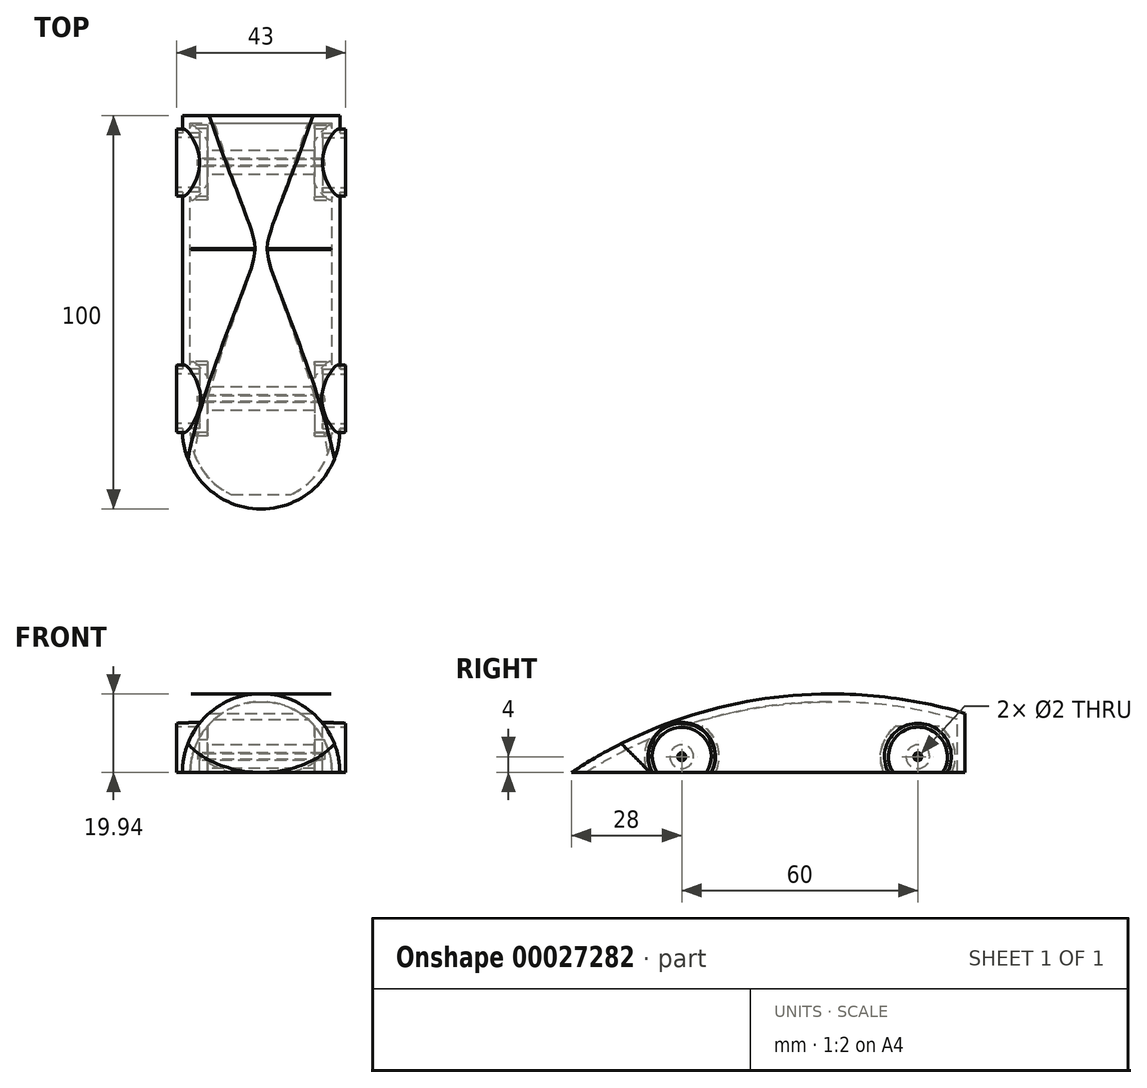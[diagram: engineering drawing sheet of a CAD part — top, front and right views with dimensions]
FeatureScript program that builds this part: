
annotation { "Feature Type Name" : "Feature", "Feature Type Description" : "" }
export const myFeature = defineFeature(function(context is Context, id is Id, definition is map)
    precondition{}
    {
        {
            var Q0;
            Q0=qCreatedBy(makeId("Top.planeOp"),FACE);
            var sketch = newSketch(context, id + "F0", { "sketchPlane" : qUnion([Q0])});
            skPoint(sketch, "E0.rect.middle", {"position": v(0, 0) * mm});
            skLineSegment(sketch, "E1.rect.bottom", {"start": v(-20, 50) * mm, "end": v(20, 50) * mm});
            skLineSegment(sketch, "E1.rect.top", {"start": v(-20, -50) * mm, "end": v(20, -50) * mm});
            skLineSegment(sketch, "E1.rect.left", {"start": v(-20, 50) * mm, "end": v(-20, -50) * mm});
            skLineSegment(sketch, "E1.rect.right", {"start": v(20, 50) * mm, "end": v(20, -50) * mm});
            skSolve(sketch);
        }
        {
            var Q0;
            Q0 = qSketchRegion(id + "F0", true);
            extrude(context, id + "F1", {"entities" : qUnion([Q0]), "depth" : 30 * mm});
        }
        {
            var Q0;
            Q0=makeQuery(id+"F1.opExtrude","SWEPT_FACE",FACE,{"disambiguationData":[OSD([sQuery(id+"F0.wireOp",EDGE,"E1.rect.top")])]});
            var sketch = newSketch(context, id + "F2", { "sketchPlane" : qUnion([Q0])});
            skArc(sketch, "E2", {"start": v(20, 15) * mm, "mid": v(0, 30) * mm, "end": v(-20, 15) * mm});
            skLineSegment(sketch, "E3", {"start": v(-20, 15) * mm, "end": v(-20, 30) * mm});
            skLineSegment(sketch, "E4", {"start": v(-20, 30) * mm, "end": v(20, 30) * mm});
            skLineSegment(sketch, "E5", {"start": v(20, 30) * mm, "end": v(20, 15) * mm});
            skSolve(sketch);
        }
        {
            var Q0;
            Q0 = qSketchRegion(id + "F2", true);
            extrude(context, id + "F3", {"entities" : qUnion([Q0]), "operationType" : NewBodyOperationType.REMOVE, "endBound" : BoundingType.THROUGH_ALL, "oppositeDirection" : true, "depth" : 25 * mm});
        }
        {
            var Q0;
            Q0=makeQuery(id+"F1.opExtrude","SWEPT_FACE",FACE,{"disambiguationData":[OSD([sQuery(id+"F0.wireOp",EDGE,"E1.rect.right")])]});
            var sketch = newSketch(context, id + "F4", { "sketchPlane" : qUnion([Q0])});
            skArc(sketch, "E6", {"start": v(50, 15) * mm, "mid": v(-1.67, 18.62) * mm, "end": v(-50, 0) * mm});
            skLineSegment(sketch, "E7.0", {"start": v(-50, 15) * mm, "end": v(-50, 30) * mm});
            skLineSegment(sketch, "E8", {"start": v(-50, 30) * mm, "end": v(50, 30) * mm});
            skLineSegment(sketch, "E9.0", {"start": v(-50, 15) * mm, "end": v(-50, 0) * mm});
            skLineSegment(sketch, "E10.0", {"start": v(50, 30) * mm, "end": v(50, 15) * mm});
            skSolve(sketch);
        }
        {
            var Q0;
            Q0 = qSketchRegion(id + "F4", true);
            extrude(context, id + "F5", {"entities" : qUnion([Q0]), "operationType" : NewBodyOperationType.REMOVE, "endBound" : BoundingType.THROUGH_ALL, "oppositeDirection" : true, "depth" : 25 * mm});
        }
        {
            var Q0;
            Q0=makeQuery(id+"F1.opExtrude","SWEPT_FACE",FACE,{"disambiguationData":[OSD([sQuery(id+"F0.wireOp",EDGE,"E1.rect.bottom")])]});
            var sketch = newSketch(context, id + "F6", { "sketchPlane" : qUnion([Q0])});
            skArc(sketch, "E11", {"start": v(20, 0) * mm, "mid": v(0, 20) * mm, "end": v(-20, 0) * mm});
            skLineSegment(sketch, "E12.0", {"start": v(-20, 15) * mm, "end": v(-20, 0) * mm});
            skLineSegment(sketch, "E13", {"start": v(-17.83, 19.94) * mm, "end": v(17.83, 19.94) * mm});
            skLineSegment(sketch, "E14.0", {"start": v(20, 15) * mm, "end": v(20, 0) * mm});
            skLineSegment(sketch, "E15", {"start": v(-20, 15) * mm, "end": v(-20, 19.94) * mm});
            skLineSegment(sketch, "E16", {"start": v(-20, 19.94) * mm, "end": v(-17.83, 19.94) * mm});
            skLineSegment(sketch, "E17", {"start": v(20, 15) * mm, "end": v(20, 19.94) * mm});
            skLineSegment(sketch, "E18", {"start": v(20, 19.94) * mm, "end": v(17.83, 19.94) * mm});
            skSolve(sketch);
        }
        {
            var Q0;
            Q0 = qSketchRegion(id + "F6", true);
            extrude(context, id + "F7", {"entities" : qUnion([Q0]), "operationType" : NewBodyOperationType.REMOVE, "endBound" : BoundingType.THROUGH_ALL, "oppositeDirection" : true, "depth" : 25 * mm});
        }
        {
            var Q0;
            Q0=makeQuery(id+"F1.opExtrude","CAP_FACE",FACE,{"disambiguationData":[OSD([sQuery(id+"F0.wireOp",EDGE,"E1.rect.bottom"),sQuery(id+"F0.wireOp",EDGE,"E1.rect.top"),sQuery(id+"F0.wireOp",EDGE,"E1.rect.left"),sQuery(id+"F0.wireOp",EDGE,"E1.rect.right")])],"isStart":true});
            var sketch = newSketch(context, id + "F8", { "sketchPlane" : qUnion([Q0])});
            skLineSegment(sketch, "E19.0", {"start": v(-20, 50) * mm, "end": v(20, 50) * mm});
            skLineSegment(sketch, "E20.0", {"start": v(-20, -50) * mm, "end": v(-20, 50) * mm});
            skLineSegment(sketch, "E21.0", {"start": v(20, -50) * mm, "end": v(20, 50) * mm});
            skArc(sketch, "E22", {"start": v(20, 30.12) * mm, "mid": v(0, 50) * mm, "end": v(-20, 30.12) * mm});
            skSolve(sketch);
        }
        {
            var Q0;
            {var subQ1=sQuery(id+"F8.wireOp",EDGE,"E19.0");var subQ3=sQuery(id+"F8.wireOp",EDGE,"E20.0");var subQ5=makeQuery(id+"F8.imprint","INTERSECT",VERTEX,{"derivedFrom":[subQ1,subQ3]});Q0=makeQuery(id+"F8.imprint","IMPRINT",FACE,{"disambiguationData":[TD([[makeQuery(id+"F8.imprint","IMPRINT",EDGE,{"disambiguationData":[TD([[subQ5,-1.0]])],"derivedFrom":subQ1}),-1.0]])]});}
            var Q1;
            {var subQ1=sQuery(id+"F8.wireOp",EDGE,"E19.0");var subQ3=sQuery(id+"F8.wireOp",EDGE,"E21.0");var subQ5=makeQuery(id+"F8.imprint","INTERSECT",VERTEX,{"derivedFrom":[subQ1,subQ3]});Q1=makeQuery(id+"F8.imprint","IMPRINT",FACE,{"disambiguationData":[TD([[makeQuery(id+"F8.imprint","IMPRINT",EDGE,{"disambiguationData":[TD([[subQ5,1.0]])],"derivedFrom":subQ1}),-1.0]])]});}
            extrude(context, id + "F9", {"entities" : qUnion([Q0, Q1]), "operationType" : NewBodyOperationType.REMOVE, "oppositeDirection" : true, "depth" : 25 * mm});
        }
        {
            var Q0;
            Q0=qCreatedBy(makeId("Right.planeOp"),FACE);
            cPlane(context, id + "F10", {"entities" : qUnion([Q0]), "cplaneType" : CPlaneType.OFFSET, "offset" : 20 * mm, "width" : 150 * mm, "height" : 150 * mm});
        }
        {
            var Q0;
            Q0=qCreatedBy(id+"F10.planeOp",FACE);
            var sketch = newSketch(context, id + "F11", { "sketchPlane" : qUnion([Q0])});
            skArc(sketch, "E23", {"start": v(45.5, 0) * mm, "mid": v(38, 12.5) * mm, "end": v(30.5, 0) * mm});
            skArc(sketch, "E24", {"start": v(-14.5, 0) * mm, "mid": v(-22, 12.5) * mm, "end": v(-29.5, 0) * mm});
            skArc(sketch, "E25.0", {"start": v(-15.66, 0) * mm, "mid": v(-22, 11.5) * mm, "end": v(-28.34, 0) * mm});
            skArc(sketch, "E26.0", {"start": v(44.34, 0) * mm, "mid": v(38, 11.5) * mm, "end": v(31.66, 0) * mm});
            skLineSegment(sketch, "E27.0", {"start": v(45.5, 0) * mm, "end": v(44.34, 0) * mm});
            skLineSegment(sketch, "E28.trimOffspring", {"start": v(31.66, 0) * mm, "end": v(30.5, 0) * mm});
            skLineSegment(sketch, "E29.trimOffspring", {"start": v(-14.5, 0) * mm, "end": v(-15.66, 0) * mm});
            skLineSegment(sketch, "E30.trimOffspring", {"start": v(-28.34, 0) * mm, "end": v(-29.5, 0) * mm});
            skPoint(sketch, "E31.orphan", {"position": v(50, 0) * mm});
            skPoint(sketch, "E32.orphan", {"position": v(-30.12, 0) * mm});
            skSolve(sketch);
        }
        {
            var Q0;
            Q0 = qSketchRegion(id + "F11", true);
            var Q1;
            {var subQ0=sQuery(id+"F6.wireOp",EDGE,"E11");var subQ1=sQuery(id+"F0.wireOp",EDGE,"E1.rect.bottom");Q1=makeQuery(id+"F7.boolean.opBoolean","COPY",FACE,{"derivedFrom":makeQuery(id+"F7.opExtrude","SWEPT_FACE",FACE,{"disambiguationData":[OSD([subQ0]),TDD([makeQuery(id+"F6.imprint","IMPRINT",EDGE,{"disambiguationData":[TD([[makeQuery(id+"F6.imprint","INTERSECT",VERTEX,{"disambiguationData":[OD(1.0)],"derivedFrom":[subQ0,sQuery(id+"F6.wireOp",EDGE,"E13")]}),-1.0]])],"derivedFrom":subQ0}),makeQuery(id+"F6.imprint","IMPRINT",EDGE,{"disambiguationData":[TD([[makeQuery(id+"F6.imprint","INTERSECT",VERTEX,{"derivedFrom":[makeQuery(id+"F1.opExtrude","CAP_EDGE",EDGE,{"disambiguationData":[OSD([subQ1])],"isStart":true}),subQ0,sQuery(id+"F6.wireOp",EDGE,"E12.0")]}),1.0]])],"derivedFrom":subQ0})])]})});}
            extrude(context, id + "F12", {"entities" : qUnion([Q0]), "operationType" : NewBodyOperationType.ADD, "endBound" : BoundingType.UP_TO_SURFACE, "oppositeDirection" : true, "endBoundEntityFace" : qUnion([Q1]), "depth" : 25 * mm, "hasSecondDirection" : true, "secondDirectionOppositeDirection" : false, "secondDirectionDepth" : 1.5 * mm});
        }
        {
            var Q0;
            Q0=qCreatedBy(id+"F10.planeOp",FACE);
            var sketch = newSketch(context, id + "F13", { "sketchPlane" : qUnion([Q0])});
            skArc(sketch, "E33.0", {"start": v(-15.66, 0) * mm, "mid": v(-22, 11.5) * mm, "end": v(-28.34, 0) * mm});
            skArc(sketch, "E34.0", {"start": v(44.34, 0) * mm, "mid": v(38, 11.5) * mm, "end": v(31.66, 0) * mm});
            skLineSegment(sketch, "E35.0", {"start": v(-15.66, 0) * mm, "end": v(-28.34, 0) * mm});
            skLineSegment(sketch, "E36.0", {"start": v(44.34, 0) * mm, "end": v(31.66, 0) * mm});
            skSolve(sketch);
        }
        {
            var Q0;
            Q0=makeQuery(id+"F1.opExtrude","SWEPT_BODY",BODY,{"disambiguationData":[OSD([sQuery(id+"F0.wireOp",EDGE,"E1.rect.bottom"),sQuery(id+"F0.wireOp",EDGE,"E1.rect.top"),sQuery(id+"F0.wireOp",EDGE,"E1.rect.left"),sQuery(id+"F0.wireOp",EDGE,"E1.rect.right")])]});
            var Q1;
            Q1=makeQuery(id+"F12.opExtrude","SWEPT_FACE",FACE,{"disambiguationData":[OSD([sQuery(id+"F11.wireOp",EDGE,"E24")])]});
            var Q2;
            Q2=makeQuery(id+"F12.opExtrude","SWEPT_FACE",FACE,{"disambiguationData":[OSD([sQuery(id+"F11.wireOp",EDGE,"E23")])]});
            var Q3;
            Q3=qCreatedBy(makeId("Right.planeOp"),FACE);
            mirror(context, id + "F14", {"operationType" : NewBodyOperationType.ADD, "entities" : qUnion([Q0]), "faces" : qUnion([Q1, Q2]), "mirrorPlane" : qUnion([Q3])});
        }
        {
            var Q0;
            Q0=makeQuery(id+"F13.imprint","IMPRINT",FACE,{"disambiguationData":[TD([[makeQuery(id+"F13.imprint","IMPRINT",EDGE,{"derivedFrom":sQuery(id+"F13.wireOp",EDGE,"E33.0")}),1.0]])]});
            var Q1;
            Q1=makeQuery(id+"F13.imprint","IMPRINT",FACE,{"disambiguationData":[TD([[makeQuery(id+"F13.imprint","IMPRINT",EDGE,{"derivedFrom":sQuery(id+"F13.wireOp",EDGE,"E34.0")}),1.0]])]});
            extrude(context, id + "F15", {"entities" : qUnion([Q0, Q1]), "operationType" : NewBodyOperationType.REMOVE, "oppositeDirection" : true, "depth" : 4.4 * mm});
        }
        {
            var Q0;
            Q0=makeQuery(id+"F14.opPattern","COPY",FACE,{"derivedFrom":makeQuery(id+"F12.opExtrude","CAP_FACE",FACE,{"disambiguationData":[OSD([sQuery(id+"F11.wireOp",EDGE,"E23"),sQuery(id+"F11.wireOp",EDGE,"E26.0"),sQuery(id+"F11.wireOp",EDGE,"E27.0"),sQuery(id+"F11.wireOp",EDGE,"E28.trimOffspring")])],"isStart":true}),"instanceName":"1"});
            var sketch = newSketch(context, id + "F16", { "sketchPlane" : qUnion([Q0])});
            skArc(sketch, "E37.0", {"start": v(-44.34, 0) * mm, "mid": v(-38, 11.5) * mm, "end": v(-31.66, 0) * mm});
            skLineSegment(sketch, "E38.0.0", {"start": v(-44.34, 0) * mm, "end": v(-31.66, 0) * mm});
            skArc(sketch, "E38.0.1", {"start": v(-31.66, 0) * mm, "mid": v(-38, 11.5) * mm, "end": v(-44.34, 0) * mm});
            skLineSegment(sketch, "E39.0", {"start": v(15.66, 0) * mm, "end": v(28.34, 0) * mm});
            skArc(sketch, "E40.0", {"start": v(15.66, 0) * mm, "mid": v(22, 11.5) * mm, "end": v(28.34, 0) * mm});
            skSolve(sketch);
        }
        {
            var Q0;
            Q0=makeQuery(id+"F16.imprint","IMPRINT",FACE,{"disambiguationData":[TD([[makeQuery(id+"F16.imprint","IMPRINT",EDGE,{"derivedFrom":sQuery(id+"F16.wireOp",EDGE,"E38.0.0")}),1.0]])]});
            var Q1;
            Q1=makeQuery(id+"F16.imprint","IMPRINT",FACE,{"disambiguationData":[TD([[makeQuery(id+"F16.imprint","IMPRINT",EDGE,{"derivedFrom":sQuery(id+"F16.wireOp",EDGE,"E39.0")}),1.0]])]});
            extrude(context, id + "F17", {"entities" : qUnion([Q0, Q1]), "operationType" : NewBodyOperationType.REMOVE, "oppositeDirection" : true, "depth" : 5.9 * mm});
        }
        {
            var Q0;
            Q0=makeQuery(id+"F17.boolean.opBoolean","COPY",FACE,{"derivedFrom":makeQuery(id+"F17.opExtrude","CAP_FACE",FACE,{"disambiguationData":[OSD([sQuery(id+"F16.wireOp",EDGE,"E38.0.0"),sQuery(id+"F16.wireOp",EDGE,"E38.0.1")])],"isStart":false})});
            var sketch = newSketch(context, id + "F18", { "sketchPlane" : qUnion([Q0])});
            skCircle(sketch, "E41", {"center": v(-38, 4) * mm, "radius": 1 * mm});
            skArc(sketch, "E42.0", {"start": v(15.66, 0) * mm, "mid": v(22, 11.5) * mm, "end": v(28.34, 0) * mm});
            skCircle(sketch, "E43", {"center": v(22, 4) * mm, "radius": 1 * mm});
            skSolve(sketch);
        }
        {
            var Q0;
            Q0 = qSketchRegion(id + "F18", true);
            extrude(context, id + "F19", {"entities" : qUnion([Q0]), "operationType" : NewBodyOperationType.REMOVE, "endBound" : BoundingType.THROUGH_ALL, "oppositeDirection" : true, "depth" : 25 * mm});
        }
        {
            var Q0;
            Q0=makeQuery(id+"F17.boolean.opBoolean","COPY",FACE,{"derivedFrom":makeQuery(id+"F17.opExtrude","CAP_FACE",FACE,{"disambiguationData":[OSD([sQuery(id+"F16.wireOp",EDGE,"E38.0.0"),sQuery(id+"F16.wireOp",EDGE,"E38.0.1")])],"isStart":false})});
            var sketch = newSketch(context, id + "F20", { "sketchPlane" : qUnion([Q0])});
            skCircle(sketch, "E44", {"center": v(-38, 4) * mm, "radius": 0.75 * mm});
            skCircle(sketch, "E45.0", {"center": v(22, 4) * mm, "radius": 1 * mm});
            skCircle(sketch, "E46", {"center": v(22, 4) * mm, "radius": 0.75 * mm});
            skSolve(sketch);
        }
        {
            var Q0;
            Q0=makeQuery(id+"F20.imprint","IMPRINT",FACE,{"disambiguationData":[TD([[makeQuery(id+"F20.imprint","IMPRINT",EDGE,{"derivedFrom":sQuery(id+"F20.wireOp",EDGE,"E44")}),1.0]])]});
            var Q1;
            Q1=makeQuery(id+"F15.boolean.opBoolean","COPY",FACE,{"derivedFrom":makeQuery(id+"F15.opExtrude","CAP_FACE",FACE,{"disambiguationData":[OSD([sQuery(id+"F13.wireOp",EDGE,"E34.0"),sQuery(id+"F13.wireOp",EDGE,"E36.0")])],"isStart":false})});
            extrude(context, id + "F21", {"entities" : qUnion([Q0]), "endBound" : BoundingType.UP_TO_SURFACE, "oppositeDirection" : true, "endBoundEntityFace" : qUnion([Q1]), "depth" : 25 * mm});
        }
        {
            var Q0;
            Q0=makeQuery(id+"F20.imprint","IMPRINT",FACE,{"disambiguationData":[TD([[makeQuery(id+"F20.imprint","IMPRINT",EDGE,{"derivedFrom":sQuery(id+"F20.wireOp",EDGE,"E46")}),1.0]])]});
            var Q1;
            Q1=makeQuery(id+"F15.boolean.opBoolean","COPY",FACE,{"derivedFrom":makeQuery(id+"F15.opExtrude","CAP_FACE",FACE,{"disambiguationData":[OSD([sQuery(id+"F13.wireOp",EDGE,"E33.0"),sQuery(id+"F13.wireOp",EDGE,"E35.0")])],"isStart":false})});
            extrude(context, id + "F22", {"entities" : qUnion([Q0]), "endBound" : BoundingType.UP_TO_SURFACE, "oppositeDirection" : true, "endBoundEntityFace" : qUnion([Q1]), "depth" : 25 * mm});
        }
        {
            var Q0;
            Q0=makeQuery(id+"F22.opExtrude","CAP_FACE",FACE,{"disambiguationData":[OSD([sQuery(id+"F20.wireOp",EDGE,"E46")])],"isStart":false});
            extrude(context, id + "F23", {"entities" : qUnion([Q0]), "operationType" : NewBodyOperationType.ADD, "depth" : .5 * mm});
        }
        {
            var Q0;
            Q0=makeQuery(id+"F22.opExtrude","CAP_FACE",FACE,{"disambiguationData":[OSD([sQuery(id+"F20.wireOp",EDGE,"E46")])],"isStart":true});
            extrude(context, id + "F24", {"entities" : qUnion([Q0]), "operationType" : NewBodyOperationType.ADD, "depth" : .5 * mm});
        }
        {
            var Q0;
            Q0=makeQuery(id+"F21.opExtrude","CAP_FACE",FACE,{"disambiguationData":[OSD([sQuery(id+"F20.wireOp",EDGE,"E44")])],"isStart":false});
            extrude(context, id + "F25", {"entities" : qUnion([Q0]), "operationType" : NewBodyOperationType.ADD, "depth" : .5 * mm});
        }
        {
            var Q0;
            Q0=makeQuery(id+"F21.opExtrude","CAP_FACE",FACE,{"disambiguationData":[OSD([sQuery(id+"F20.wireOp",EDGE,"E44")])],"isStart":true});
            extrude(context, id + "F26", {"entities" : qUnion([Q0]), "operationType" : NewBodyOperationType.ADD, "depth" : .5 * mm});
        }
        {
            var Q0;
            Q0=qCreatedBy(makeId("Right.planeOp"),FACE);
            var sketch = newSketch(context, id + "F27", { "sketchPlane" : qUnion([Q0])});
            skArc(sketch, "E47.0", {"start": v(-14.5, 0) * mm, "mid": v(-22, 12.5) * mm, "end": v(-29.5, 0) * mm});
            skArc(sketch, "E48.0", {"start": v(-37.34, 7.34) * mm, "mid": v(5.6, 19.48) * mm, "end": v(50, 15) * mm});
            skArc(sketch, "E49", {"start": v(-13.75, 0) * mm, "mid": v(-22, 13.16) * mm, "end": v(-30.25, 0) * mm});
            skLineSegment(sketch, "E50", {"start": v(-13.75, 0) * mm, "end": v(-14.5, 0) * mm});
            skLineSegment(sketch, "E51.trimOffspring", {"start": v(-29.5, 0) * mm, "end": v(-30.25, 0) * mm});
            skSolve(sketch);
        }
        {
            var Q1;
            Q1=makeQuery(id+"F12.opExtrude","CAP_FACE",FACE,{"disambiguationData":[OSD([sQuery(id+"F11.wireOp",EDGE,"E24"),sQuery(id+"F11.wireOp",EDGE,"E25.0"),sQuery(id+"F11.wireOp",EDGE,"E29.trimOffspring"),sQuery(id+"F11.wireOp",EDGE,"E30.trimOffspring")])],"isStart":true});
            var Q2;
            Q2 = qSketchRegion(id + "F27", true);
            var Q3;
            Q3=makeQuery(id+"F14.opPattern","COPY",FACE,{"derivedFrom":makeQuery(id+"F12.opExtrude","CAP_FACE",FACE,{"disambiguationData":[OSD([sQuery(id+"F11.wireOp",EDGE,"E24"),sQuery(id+"F11.wireOp",EDGE,"E25.0"),sQuery(id+"F11.wireOp",EDGE,"E29.trimOffspring"),sQuery(id+"F11.wireOp",EDGE,"E30.trimOffspring")])],"isStart":true}),"instanceName":"1"});
            loft(context, id + "F28", {"operationType" : NewBodyOperationType.ADD, "sheetProfilesArray" : [{ "sheetProfileEntities" : qUnion([Q1]) }, { "sheetProfileEntities" : qUnion([Q2]) }, { "sheetProfileEntities" : qUnion([Q3]) }]});
        }
        {
            var Q0;
            {var subQ0=sQuery(id+"F11.wireOp",EDGE,"E29.trimOffspring");var subQ1=sQuery(id+"F11.wireOp",EDGE,"E30.trimOffspring");var subQ2=makeQuery(id+"F12.boolean.opBoolean","MERGE",FACE,{"derivedFrom":[makeQuery(id+"F1.opExtrude","CAP_FACE",FACE,{"disambiguationData":[OSD([sQuery(id+"F0.wireOp",EDGE,"E1.rect.bottom"),sQuery(id+"F0.wireOp",EDGE,"E1.rect.top"),sQuery(id+"F0.wireOp",EDGE,"E1.rect.left"),sQuery(id+"F0.wireOp",EDGE,"E1.rect.right")])],"isStart":true}),makeQuery(id+"F12.opExtrude","SWEPT_FACE",FACE,{"disambiguationData":[OSD([sQuery(id+"F11.wireOp",EDGE,"E27.0")])]}),makeQuery(id+"F12.opExtrude","SWEPT_FACE",FACE,{"disambiguationData":[OSD([sQuery(id+"F11.wireOp",EDGE,"E28.trimOffspring")])]}),makeQuery(id+"F12.opExtrude","SWEPT_FACE",FACE,{"disambiguationData":[OSD([subQ0])]}),makeQuery(id+"F12.opExtrude","SWEPT_FACE",FACE,{"disambiguationData":[OSD([subQ1])]})]});var subQ3=sQuery(id+"F11.wireOp",EDGE,"E24");var subQ4=sQuery(id+"F11.wireOp",EDGE,"E25.0");var subQ5=sQuery(id+"F27.wireOp",EDGE,"E47.0");var subQ6=sQuery(id+"F27.wireOp",EDGE,"E49");Q0=makeQuery(id+"F28.boolean.opBoolean","MERGE",FACE,{"derivedFrom":[makeQuery(id+"F14.boolean.opBoolean","MERGE",FACE,{"derivedFrom":[subQ2,makeQuery(id+"F14.opPattern","COPY",FACE,{"derivedFrom":subQ2,"instanceName":"1"})]}),makeQuery(id+"F28.opLoft","SWEPT_FACE",FACE,{"disambiguationData":[OSD([subQ3,subQ4,subQ0,subQ5,subQ6,sQuery(id+"F27.wireOp",EDGE,"E50")])]}),makeQuery(id+"F28.opLoft","SWEPT_FACE",FACE,{"disambiguationData":[OSD([subQ3,subQ4,subQ1,subQ5,subQ6,sQuery(id+"F27.wireOp",EDGE,"E51.trimOffspring")])]})]});}
            shell(context, id + "F29", {"entities" : qUnion([Q0]), "thickness" : 2 * mm});
        }
    });
